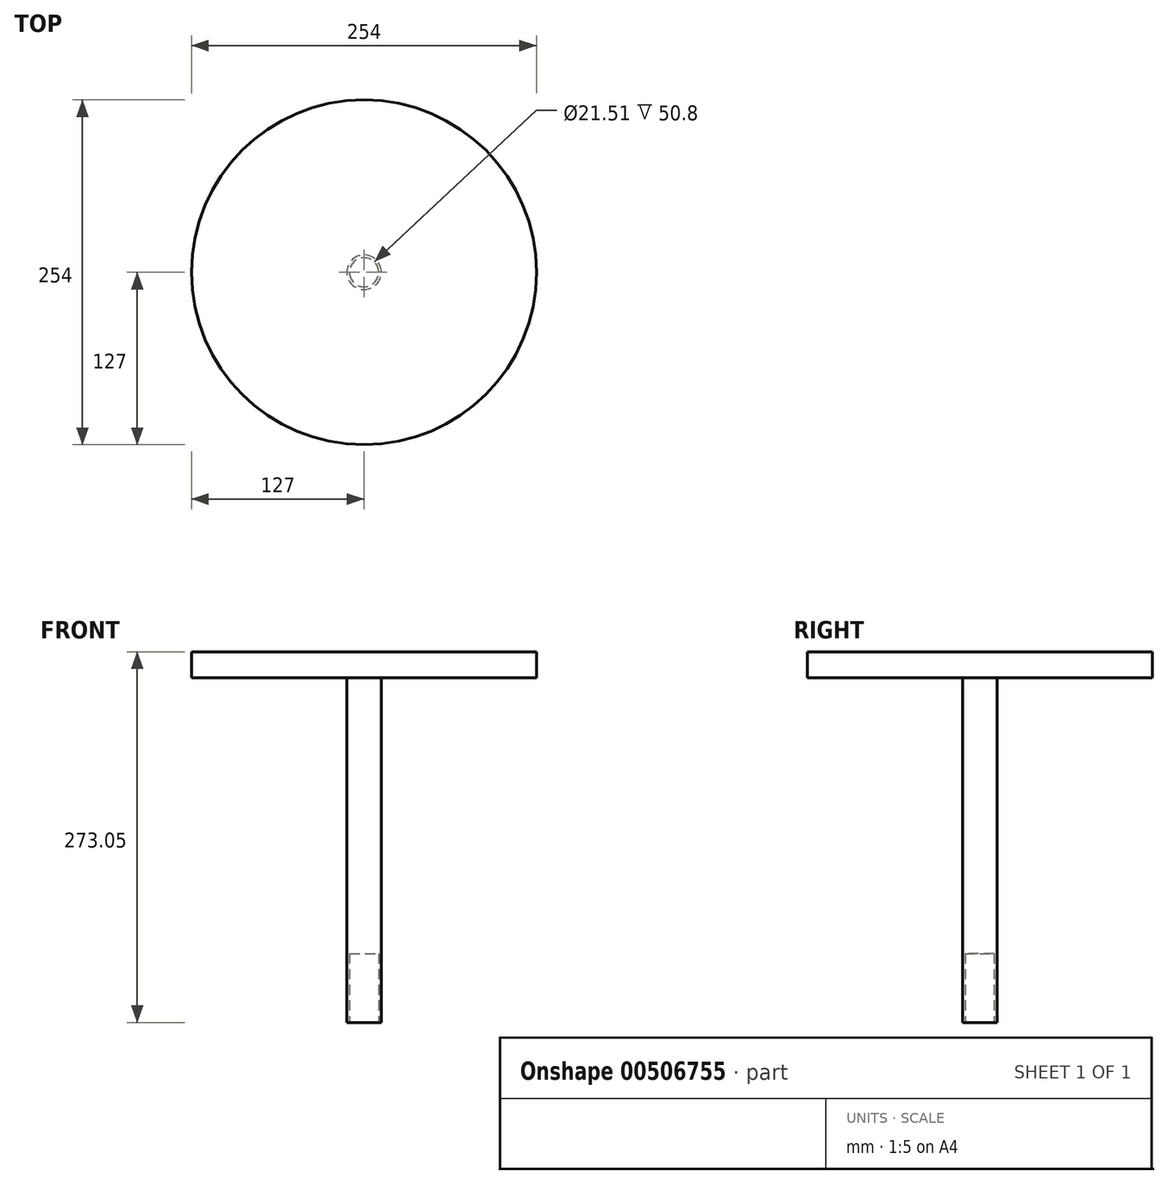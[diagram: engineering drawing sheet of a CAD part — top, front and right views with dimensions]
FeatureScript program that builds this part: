
annotation { "Feature Type Name" : "Feature", "Feature Type Description" : "" }
export const myFeature = defineFeature(function(context is Context, id is Id, definition is map)
    precondition{}
    {
        {
            var Q0;
            Q0=qCreatedBy(makeId("Top.planeOp"),FACE);
            var sketch = newSketch(context, id + "F0", { "sketchPlane" : qUnion([Q0])});
            skCircle(sketch, "E0", {"center": v(0, 0) * mm, "radius": 127 * mm});
            skSolve(sketch);
        }
        {
            var Q0;
            Q0=makeQuery(id+"F0.imprint","IMPRINT",FACE,{"disambiguationData":[TD([[makeQuery(id+"F0.imprint","IMPRINT",EDGE,{"derivedFrom":sQuery(id+"F0.wireOp",EDGE,"E0")}),1.0]])]});
            extrude(context, id + "F1", {"entities" : qUnion([Q0]), "depth" : 19.05 * mm});
        }
        {
            var Q0;
            Q0=makeQuery(id+"F1.opExtrude","CAP_FACE",FACE,{"disambiguationData":[OSD([sQuery(id+"F0.wireOp",EDGE,"E0")])],"isStart":true});
            var sketch = newSketch(context, id + "F2", { "sketchPlane" : qUnion([Q0])});
            skCircle(sketch, "E1", {"center": v(0, 0) * mm, "radius": 12.7 * mm});
            skSolve(sketch);
        }
        {
            var Q0;
            Q0=makeQuery(id+"F2.imprint","IMPRINT",FACE,{"disambiguationData":[TD([[makeQuery(id+"F2.imprint","IMPRINT",EDGE,{"derivedFrom":sQuery(id+"F2.wireOp",EDGE,"E1")}),1.0]])]});
            extrude(context, id + "F3", {"entities" : qUnion([Q0]), "operationType" : NewBodyOperationType.ADD, "depth" : 254 * mm, "offsetDistance" : 25.4 * mm});
        }
        {
            var Q0;
            Q0=makeQuery(id+"F3.opExtrude","CAP_FACE",FACE,{"disambiguationData":[OSD([sQuery(id+"F2.wireOp",EDGE,"E1")])],"isStart":false});
            var sketch = newSketch(context, id + "F4", { "sketchPlane" : qUnion([Q0])});
            skCircle(sketch, "E2.0", {"center": v(0, 0) * mm, "radius": 10.76 * mm});
            skCircle(sketch, "E3.0", {"center": v(0, 0) * mm, "radius": 19.05 * mm});
            skSolve(sketch);
        }
        {
            var Q0;
            Q0=makeQuery(id+"F4.imprint","IMPRINT",FACE,{"disambiguationData":[TD([[makeQuery(id+"F4.imprint","IMPRINT",EDGE,{"derivedFrom":sQuery(id+"F4.wireOp",EDGE,"E2.0")}),1.0]])]});
            extrude(context, id + "F5", {"entities" : qUnion([Q0]), "operationType" : NewBodyOperationType.REMOVE, "oppositeDirection" : true, "depth" : 50.8 * mm});
        }
    });
